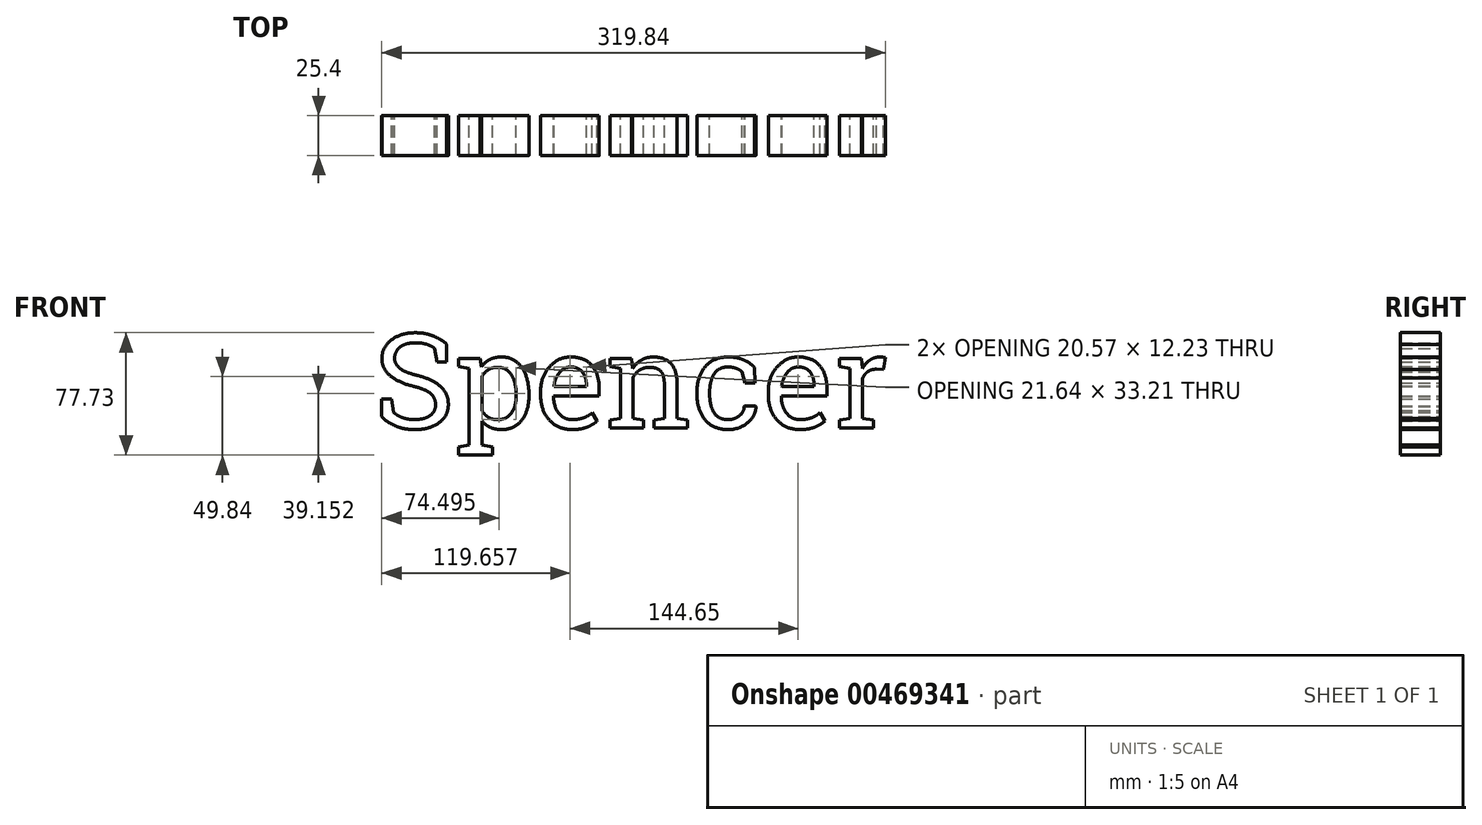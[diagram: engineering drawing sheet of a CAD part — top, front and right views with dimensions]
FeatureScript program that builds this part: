
annotation { "Feature Type Name" : "Feature", "Feature Type Description" : "" }
export const myFeature = defineFeature(function(context is Context, id is Id, definition is map)
    precondition{}
    {
        {
            var Q0;
            Q0=qCreatedBy(makeId("Front.planeOp"),FACE);
            var sketch = newSketch(context, id + "F0", { "sketchPlane" : qUnion([Q0])});
            skText(sketch, "E0", { "text": "Spencer", "fontName": "RobotoSlab-Regular.ttf"});
            const initialGuessF0  = {"E0": [-0.18008, 0.01533, 1, 0, 0.06054]};
            skSetInitialGuess(sketch, initialGuessF0);
            skSolve(sketch);
        }
        {
            var Q0;
            Q0 = qSketchRegion(id + "F0", true);
            extrude(context, id + "F1", {"entities" : qUnion([Q0]), "depth" : 25.4 * mm});
        }
    });
